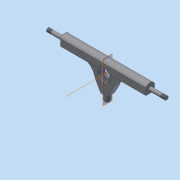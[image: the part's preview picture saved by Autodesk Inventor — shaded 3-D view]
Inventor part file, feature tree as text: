
AUTODESK INVENTOR PART (.ipt)
format: ipt  version: 2017 (Build 210142000, 142)  size: 207,360 bytes
history: native  units: in
note: dims shown in document units (in); Inventor stores cm internally (conversion verified against a paired STEP export)
features: extrude x7, plane x6, sketch x5, fillet x4, mirror x2, thread x2, other x2
ambient origin geometry x8: Origin, YZ Plane, XZ Plane, XY Plane, X Axis, Y Axis, Z Axis, Center Point
bodies: Solid1 (feature_tree)
feature tree (28):
  extrude  "Truck Axle"  Depth=0.72in
  extrude  "Axle"  Depth=1.375in TaperAngle=0.0deg
  plane  "Work Plane1"
  mirror  "Other Axle"
  plane  "Work Plane3"
  extrude  "Pentagon"  Depth=1.0in
  fillet  "Fillet1"  Radius=1.0in
  sketch  "Sketch6"  dims[d31=2.0in d32=0.0in d37=0.65in d38=0.0in]
  extrude  "Inner hole"  Depth=0.65in TaperAngle=0.0deg
  extrude  "Middle hole"  Depth=0.41in
  extrude  "Outer hole"  Depth=0.41in TaperAngle=0.0deg
  extrude  "Ball joint"  Depth=0.41in TaperAngle=0.0deg
  fillet  "Fillet3"  Radius=0.5in
  thread  "Thread3"  [1 undecoded]
  thread  "Thread4"  [1 undecoded]
  fillet  "Fillet6"  Radius=5.0in
  plane  "Work Plane4"
  mirror  "Mirror2"
  fillet  "Fillet7"  Radius=0.65in
  other  "Work Point1"
  plane  "Work Plane6"
  sketch  "Sketch1"  dims[d0=0.56in d1=0.72in]
  sketch  "Sketch2"  dims[d6=7.2047in d7=0.0in d8=1.375in d9=0.0in]
  plane  "Work Plane2"
  sketch  "Sketch4"  dims[d19=0.5512in d20=0.0in d25=0.55in d29=1.0in]
  sketch  "Sketch10"  dims[d39=0.05in d40=0.3125in d41=0.375in d42=0.0in d43=0.375in d44=0.0in d45=0.5in d49=1.8in d50=1.6in d53=5.0in d54=0.65in d56=1.0in d57=1.1811in d58=1.0in d59=0.0in d60=0.1772in d61=0.0in d62=1.0in d63=0.0984in d64=0.0in d65=0.0in d67=1.4961in d68=0.25in d70=1.0in d72=0.41in d73=0.3287in]
  other  "Work Axis1"
  plane  "Work Plane5"
note: 2 required parameter values undecoded (feature->parameter linkage not recoverable at this tier; creation-order binding heuristic only, values carry confidence <= 0.55)
